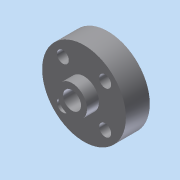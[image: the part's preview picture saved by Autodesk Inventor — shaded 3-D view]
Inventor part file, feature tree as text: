
AUTODESK INVENTOR PART (.ipt)
format: ipt  version: 2012 (Build 160160000, 160)  size: 129,024 bytes
history: native  units: in
note: dims shown in document units (in); Inventor stores cm internally (conversion verified against a paired STEP export)
features: sketch x5, extrude x4, hole x1, pattern_circular x1
ambient origin geometry x8: Origin, YZ Plane, XZ Plane, XY Plane, X Axis, Y Axis, Z Axis, Center Point
bodies: Solid1 (feature_tree)
feature tree (11):
  extrude  "Extrusion1"  Depth=0.1875in
  extrude  "Extrusion2"  Depth=0.3125in
  extrude  "Extrusion3"  Depth=0.25in TaperAngle=0.0deg
  hole  "Hole2"  [1 undecoded]
  pattern_circular  "Circular Pattern1"  Count=4 Angle=360.0deg
  extrude  "Extrusion4"  Depth=0.125in
  sketch  "Sketch1"  dims[d0=0.875in d1=0.1875in]
  sketch  "Sketch2"  dims[d2=0.125in d3=0.3125in]
  sketch  "Sketch4"  dims[d4=1.5748in d6=360.0deg d8=0.25in d9=0.0in]
  sketch  "Sketch5"  dims[d10=0.3125in d11=0.125in d12=0.0in d20=1.5748in d22=360.0deg]
  sketch  "Sketch6"  dims[d24=0.25in d25=0.0in d26=0.125in d27=0.3125in d28=0.125in d29=0.75in d30=0.375in d31=0.25in d32=0.5635in d33=1.0in d34=0.8108in d35=3.1496in d36=360.0deg d38=1.5748in d40=360.0deg d42=0.25in d43=0.0in]
note: 1 required parameter value undecoded (feature->parameter linkage not recoverable at this tier; creation-order binding heuristic only, values carry confidence <= 0.55)
